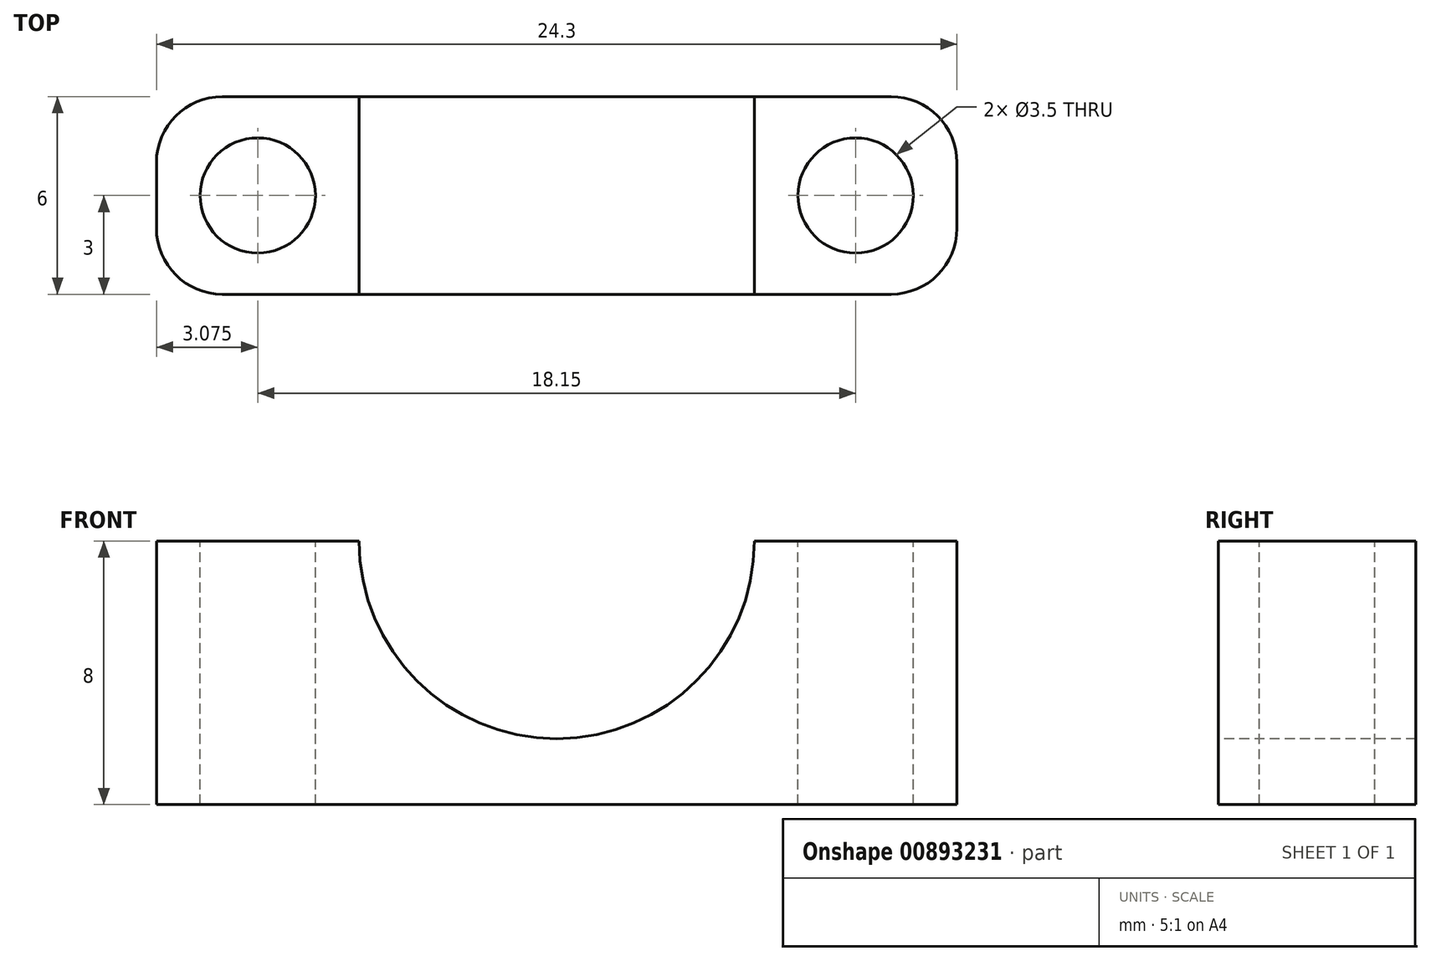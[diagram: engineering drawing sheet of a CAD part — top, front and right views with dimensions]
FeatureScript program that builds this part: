
annotation { "Feature Type Name" : "Feature", "Feature Type Description" : "" }
export const myFeature = defineFeature(function(context is Context, id is Id, definition is map)
    precondition{}
    {
        {
            var Q0;
            Q0=qCreatedBy(makeId("Top.planeOp"),FACE);
            var sketch = newSketch(context, id + "F0", { "sketchPlane" : qUnion([Q0])});
            skLineSegment(sketch, "E0.bottom", {"start": v(12.15, 3) * mm, "end": v(-12.15, 3) * mm});
            skLineSegment(sketch, "E0.top", {"start": v(12.15, -3) * mm, "end": v(-12.15, -3) * mm});
            skLineSegment(sketch, "E0.left", {"start": v(12.15, 3) * mm, "end": v(12.15, -3) * mm});
            skLineSegment(sketch, "E0.right", {"start": v(-12.15, 3) * mm, "end": v(-12.15, -3) * mm});
            skPoint(sketch, "E0.middle", {"position": v(0, 0) * mm});
            skSolve(sketch);
        }
        {
            var Q0;
            Q0 = qSketchRegion(id + "F0", true);
            extrude(context, id + "F1", {"entities" : qUnion([Q0]), "depth" : 8 * mm, "offsetDistance" : 25 * mm});
        }
        {
            var Q0;
            Q0=makeQuery(id+"F1.opExtrude","SWEPT_FACE",FACE,{"disambiguationData":[OSD([sQuery(id+"F0.wireOp",EDGE,"E0.top")])]});
            var sketch = newSketch(context, id + "F2", { "sketchPlane" : qUnion([Q0])});
            skCircle(sketch, "E1", {"center": v(0, 8) * mm, "radius": 6 * mm});
            skSolve(sketch);
        }
        {
            var Q0;
            Q0 = qSketchRegion(id + "F2", true);
            extrude(context, id + "F3", {"entities" : qUnion([Q0]), "operationType" : NewBodyOperationType.REMOVE, "endBound" : BoundingType.THROUGH_ALL, "oppositeDirection" : true, "depth" : 25 * mm, "offsetDistance" : 25 * mm});
        }
        {
            var Q0;
            {var subQ0=sQuery(id+"F0.wireOp",EDGE,"E0.bottom");var subQ1=sQuery(id+"F0.wireOp",EDGE,"E0.right");var subQ2=sQuery(id+"F0.wireOp",EDGE,"E0.top");Q0=makeQuery(id+"F3.boolean.opBoolean","SPLIT",FACE,{"disambiguationData":[TD([makeQuery(id+"F1.opExtrude","SWEPT_FACE",FACE,{"disambiguationData":[OSD([subQ1])]})])],"derivedFrom":makeQuery(id+"F1.opExtrude","CAP_FACE",FACE,{"disambiguationData":[OSD([subQ0,subQ2,sQuery(id+"F0.wireOp",EDGE,"E0.left"),subQ1])],"isStart":false})});}
            var sketch = newSketch(context, id + "F4", { "sketchPlane" : qUnion([Q0])});
            skLineSegment(sketch, "E2", {"start": v(-12.15, 3) * mm, "end": v(-6, -3) * mm, "construction": true});
            skLineSegment(sketch, "E3", {"start": v(-6, 3) * mm, "end": v(-12.15, -3) * mm, "construction": true});
            skPoint(sketch, "E4", {"position": v(-9.07, 0) * mm});
            skCircle(sketch, "E5", {"center": v(-9.07, 0) * mm, "radius": 1.75 * mm});
            skCircle(sketch, "E6.MirrorC", {"center": v(9.07, 0) * mm, "radius": 1.75 * mm});
            skSolve(sketch);
        }
        {
            var Q0;
            Q0 = qSketchRegion(id + "F4", true);
            extrude(context, id + "F5", {"entities" : qUnion([Q0]), "operationType" : NewBodyOperationType.REMOVE, "endBound" : BoundingType.THROUGH_ALL, "oppositeDirection" : true, "depth" : 25 * mm, "offsetDistance" : 25 * mm});
        }
        {
            var Q0;
            Q0=makeQuery(id+"F1.opExtrude","SWEPT_EDGE",EDGE,{"disambiguationData":[OSD([sQuery(id+"F0.wireOp",EDGE,"E0.top"),sQuery(id+"F0.wireOp",EDGE,"E0.right")])]});
            var Q1;
            Q1=makeQuery(id+"F1.opExtrude","SWEPT_EDGE",EDGE,{"disambiguationData":[OSD([sQuery(id+"F0.wireOp",EDGE,"E0.bottom"),sQuery(id+"F0.wireOp",EDGE,"E0.right")])]});
            var Q2;
            Q2=makeQuery(id+"F1.opExtrude","SWEPT_EDGE",EDGE,{"disambiguationData":[OSD([sQuery(id+"F0.wireOp",EDGE,"E0.top"),sQuery(id+"F0.wireOp",EDGE,"E0.left")])]});
            var Q3;
            Q3=makeQuery(id+"F1.opExtrude","SWEPT_EDGE",EDGE,{"disambiguationData":[OSD([sQuery(id+"F0.wireOp",EDGE,"E0.bottom"),sQuery(id+"F0.wireOp",EDGE,"E0.left")])]});
            fillet(context, id + "F6", {"entities" : qUnion([Q0, Q1, Q2, Q3]), "radius" : 2 * mm, "tangentPropagation" : true, "allowEdgeOverflow" : false});
        }
    });
